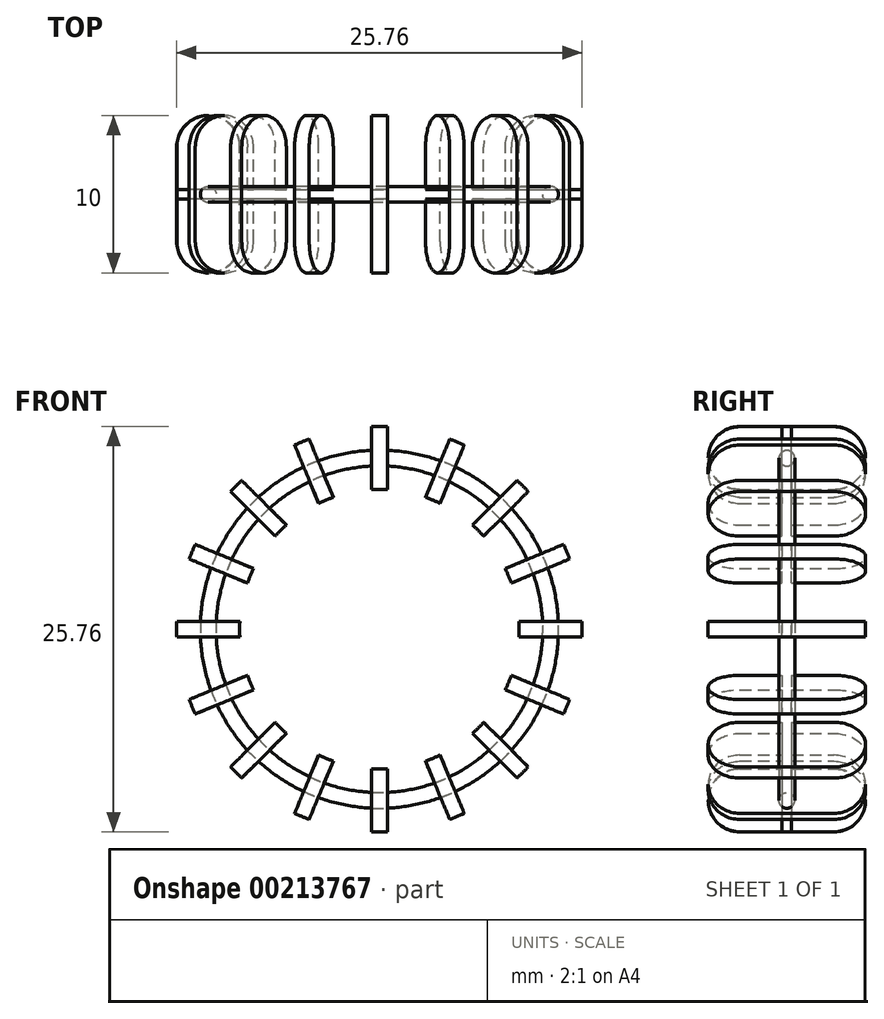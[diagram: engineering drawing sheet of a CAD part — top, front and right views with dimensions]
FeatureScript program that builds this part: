
annotation { "Feature Type Name" : "Feature", "Feature Type Description" : "" }
export const myFeature = defineFeature(function(context is Context, id is Id, definition is map)
    precondition{}
    {
        {
            var Q0;
            Q0=qCreatedBy(makeId("Front.planeOp"),FACE);
            var sketch = newSketch(context, id + "F0", { "sketchPlane" : qUnion([Q0])});
            skArc(sketch, "E0", {"start": v(0.5, 8.86) * mm, "mid": v(0, 8.88) * mm, "end": v(-0.5, 8.86) * mm});
            skArc(sketch, "E1.0", {"start": v(0.5, 12.87) * mm, "mid": v(0, 12.88) * mm, "end": v(-0.5, 12.87) * mm});
            skCircle(sketch, "E2.0", {"center": v(0, 0) * mm, "radius": 10.88 * mm, "construction": true});
            skCircle(sketch, "E3.0", {"center": v(0, 0) * mm, "radius": 11.38 * mm});
            skCircle(sketch, "E4.0", {"center": v(0, 0) * mm, "radius": 10.38 * mm});
            skLineSegment(sketch, "E5", {"start": v(0.5, 12.87) * mm, "end": v(0.5, 8.86) * mm});
            skLineSegment(sketch, "E6.MirrorCS", {"start": v(-0.5, 12.87) * mm, "end": v(-0.5, 8.86) * mm});
            skSolve(sketch);
        }
        {
            var Q0;
            Q0=makeQuery(id+"F0.imprint","IMPRINT",FACE,{"disambiguationData":[TD([[makeQuery(id+"F0.imprint","IMPRINT",EDGE,{"derivedFrom":sQuery(id+"F0.wireOp",EDGE,"E0")}),-1.0]])]});
            var Q1;
            {var subQ0=sQuery(id+"F0.wireOp",EDGE,"E1.0");Q1=makeQuery(id+"F0.imprint","IMPRINT",FACE,{"disambiguationData":[TD([[makeQuery(id+"F0.imprint","IMPRINT",EDGE,{"derivedFrom":subQ0}),1.0]])]});}
            var Q2;
            {var subQ0=sQuery(id+"F0.wireOp",EDGE,"E5");var subQ1=sQuery(id+"F0.wireOp",EDGE,"E3.0");var subQ2=makeQuery(id+"F0.imprint","INTERSECT",VERTEX,{"derivedFrom":[subQ1,subQ0]});Q2=makeQuery(id+"F0.imprint","IMPRINT",FACE,{"disambiguationData":[TD([[makeQuery(id+"F0.imprint","IMPRINT",EDGE,{"disambiguationData":[TD([[subQ2,-1.0]])],"derivedFrom":subQ1}),1.0]])]});}
            extrude(context, id + "F1", {"entities" : qUnion([Q0, Q1, Q2]), "depth" : 5 * mm, "hasSecondDirection" : true, "secondDirectionOppositeDirection" : true, "secondDirectionDepth" : 5 * mm});
        }
        {
            var Q0;
            Q0=makeQuery(id+"F1.opExtrude","CAP_EDGE",EDGE,{"disambiguationData":[OSD([sQuery(id+"F0.wireOp",EDGE,"E1.0")])],"isStart":false});
            var Q1;
            Q1=makeQuery(id+"F1.opExtrude","CAP_EDGE",EDGE,{"disambiguationData":[OSD([sQuery(id+"F0.wireOp",EDGE,"E0")])],"isStart":false});
            var Q2;
            Q2=makeQuery(id+"F1.opExtrude","CAP_EDGE",EDGE,{"disambiguationData":[OSD([sQuery(id+"F0.wireOp",EDGE,"E1.0")])],"isStart":true});
            var Q3;
            Q3=makeQuery(id+"F1.opExtrude","CAP_EDGE",EDGE,{"disambiguationData":[OSD([sQuery(id+"F0.wireOp",EDGE,"E0")])],"isStart":true});
            fillet(context, id + "F2", {"entities" : qUnion([Q0, Q1, Q2, Q3]), "radius" : 2 * mm, "tangentPropagation" : true, "allowEdgeOverflow" : false});
        }
        {
            var Q0;
            Q0=qCreatedBy(makeId("Right.planeOp"),FACE);
            var sketch = newSketch(context, id + "F3", { "sketchPlane" : qUnion([Q0])});
            skLineSegment(sketch, "E7", {"start": v(0.3, 12.87) * mm, "end": v(0.3, 8.86) * mm});
            skLineSegment(sketch, "E8.MirrorCS", {"start": v(-0.3, 12.87) * mm, "end": v(-0.3, 8.86) * mm});
            skLineSegment(sketch, "E9", {"start": v(-0.3, 12.87) * mm, "end": v(0.3, 12.87) * mm});
            skLineSegment(sketch, "E10", {"start": v(-0.3, 8.86) * mm, "end": v(0.3, 8.86) * mm});
            skSolve(sketch);
        }
        {
            var Q0;
            Q0=makeQuery(id+"F3.imprint","IMPRINT",FACE,{"disambiguationData":[TD([[makeQuery(id+"F3.imprint","IMPRINT",EDGE,{"derivedFrom":sQuery(id+"F3.wireOp",EDGE,"E7")}),-1.0]])]});
            extrude(context, id + "F4", {"entities" : qUnion([Q0]), "operationType" : NewBodyOperationType.REMOVE, "depth" : 2 * mm, "hasSecondDirection" : true, "secondDirectionOppositeDirection" : true, "secondDirectionDepth" : 2 * mm});
        }
        {
            var Q0;
            Q0=makeQuery(id+"F3.imprint","IMPRINT",FACE,{"disambiguationData":[TD([[makeQuery(id+"F3.imprint","IMPRINT",EDGE,{"derivedFrom":sQuery(id+"F3.wireOp",EDGE,"E7")}),-1.0]])]});
            extrude(context, id + "F5", {"entities" : qUnion([Q0]), "operationType" : NewBodyOperationType.REMOVE, "oppositeDirection" : true, "depth" : 2 * mm, "hasSecondDirection" : true, "secondDirectionOppositeDirection" : true, "secondDirectionDepth" : .3 * mm});
        }
        {
            var Q0;
            Q0=makeQuery(id+"F1.opExtrude","SWEPT_BODY",BODY,{"disambiguationData":[OSD([sQuery(id+"F0.wireOp",EDGE,"E0"),sQuery(id+"F0.wireOp",EDGE,"E1.0"),sQuery(id+"F0.wireOp",EDGE,"E5"),sQuery(id+"F0.wireOp",EDGE,"E6.MirrorCS")])]});
            var Q1;
            Q1=sQuery(id+"F0.wireOp",EDGE,"E2.0");
            circularPattern(context, id + "F6", {"entities" : qUnion([Q0]), "axis" : qUnion([Q1]), "angle" : 360 * degree, "instanceCount" : 16, "equalSpace" : true});
        }
        {
            var Q0;
            {var subQ0=sQuery(id+"F0.wireOp",EDGE,"E5");var subQ1=sQuery(id+"F0.wireOp",EDGE,"E3.0");var subQ2=makeQuery(id+"F0.imprint","INTERSECT",VERTEX,{"derivedFrom":[subQ1,subQ0]});Q0=makeQuery(id+"F0.imprint","IMPRINT",FACE,{"disambiguationData":[TD([[makeQuery(id+"F0.imprint","IMPRINT",EDGE,{"disambiguationData":[TD([[subQ2,1.0]])],"derivedFrom":subQ1}),1.0]])]});}
            extrude(context, id + "F7", {"entities" : qUnion([Q0]), "depth" : .5 * mm, "hasSecondDirection" : true, "secondDirectionOppositeDirection" : true, "secondDirectionDepth" : .5 * mm});
        }
        {
            var Q0;
            Q0=makeQuery(id+"F7.opExtrude","CAP_EDGE",EDGE,{"disambiguationData":[OSD([sQuery(id+"F0.wireOp",EDGE,"E3.0")])],"isStart":true});
            var Q1;
            Q1=makeQuery(id+"F7.opExtrude","CAP_EDGE",EDGE,{"disambiguationData":[OSD([sQuery(id+"F0.wireOp",EDGE,"E3.0")])],"isStart":false});
            var Q2;
            Q2=makeQuery(id+"F7.opExtrude","CAP_EDGE",EDGE,{"disambiguationData":[OSD([sQuery(id+"F0.wireOp",EDGE,"E4.0")])],"isStart":false});
            var Q3;
            Q3=makeQuery(id+"F7.opExtrude","CAP_EDGE",EDGE,{"disambiguationData":[OSD([sQuery(id+"F0.wireOp",EDGE,"E4.0")])],"isStart":true});
            fillet(context, id + "F8", {"entities" : qUnion([Q0, Q1, Q2, Q3]), "radius" : .5 * mm, "tangentPropagation" : true, "allowEdgeOverflow" : false});
        }
    });
